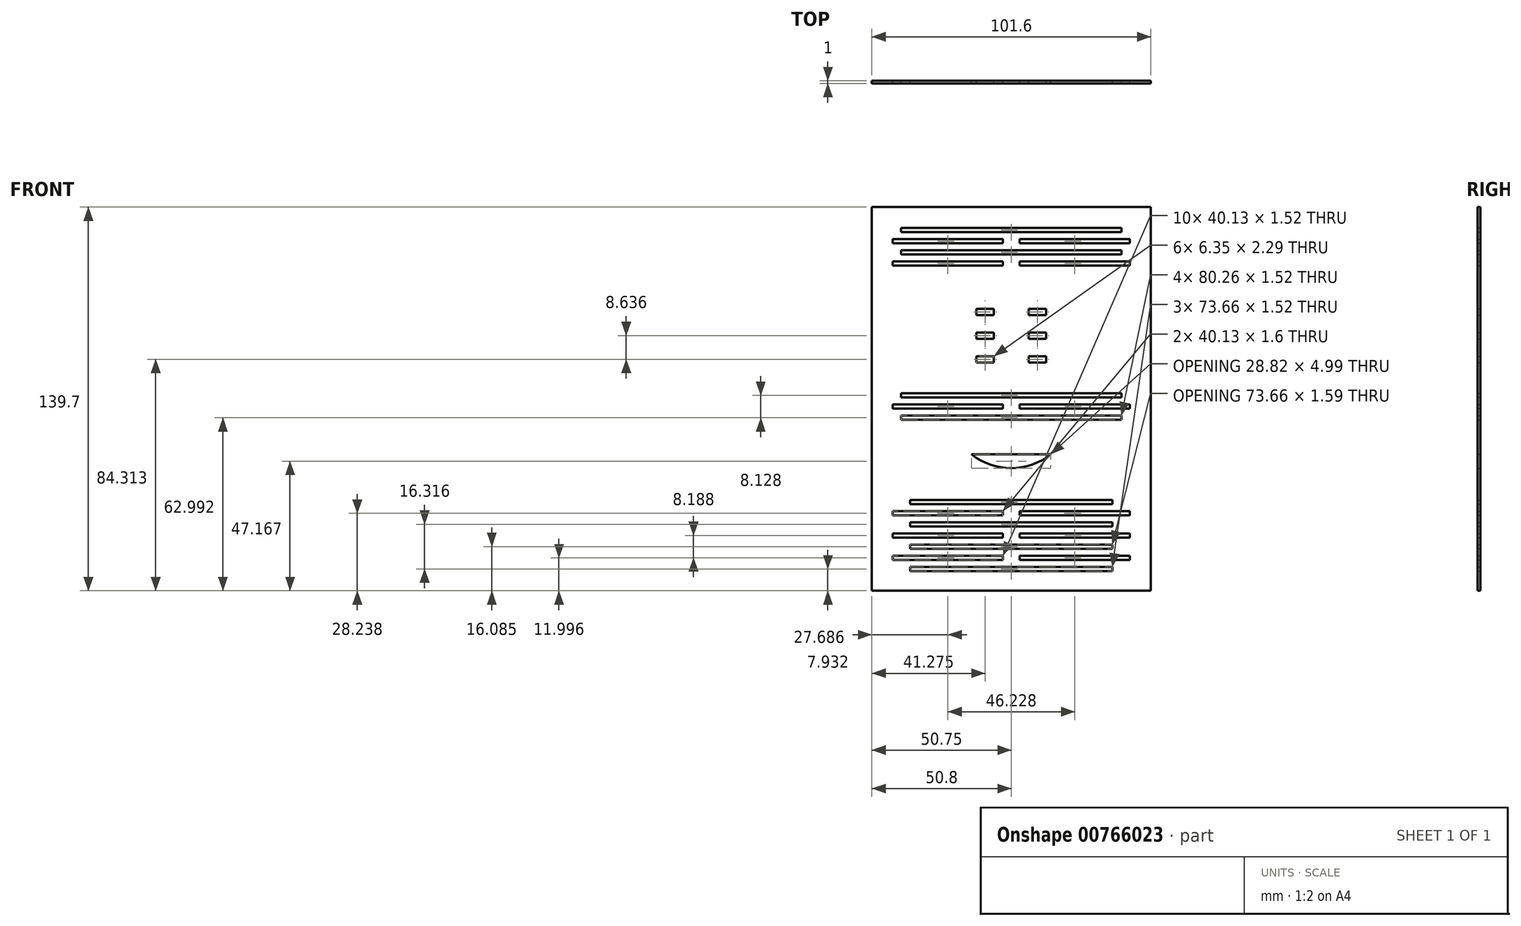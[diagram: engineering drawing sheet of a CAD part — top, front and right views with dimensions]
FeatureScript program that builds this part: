
annotation { "Feature Type Name" : "Feature", "Feature Type Description" : "" }
export const myFeature = defineFeature(function(context is Context, id is Id, definition is map)
    precondition{}
    {
        {
            var Q0;
            Q0=qCreatedBy(makeId("Front.planeOp"),FACE);
            var sketch = newSketch(context, id + "F0", { "sketchPlane" : qUnion([Q0])});
            skLineSegment(sketch, "E0.bottom", {"start": v(-50.8, 69.85) * mm, "end": v(50.8, 69.85) * mm});
            skLineSegment(sketch, "E0.top", {"start": v(-50.8, -69.85) * mm, "end": v(50.8, -69.85) * mm});
            skLineSegment(sketch, "E0.left", {"start": v(-50.8, 69.85) * mm, "end": v(-50.8, -69.85) * mm});
            skLineSegment(sketch, "E0.right", {"start": v(50.8, 69.85) * mm, "end": v(50.8, -69.85) * mm});
            skPoint(sketch, "E0.middle", {"position": v(0, 0) * mm});
            skLineSegment(sketch, "E1", {"start": v(-43.18, 62.23) * mm, "end": v(-43.18, -7.62) * mm});
            skLineSegment(sketch, "E2", {"start": v(43.18, 62.23) * mm, "end": v(43.18, -7.62) * mm});
            skLineSegment(sketch, "E3", {"start": v(-43.18, -20.19) * mm, "end": v(-43.18, -62.68) * mm});
            skLineSegment(sketch, "E4", {"start": v(-43.18, -20.19) * mm, "end": v(43.18, -20.19) * mm});
            skLineSegment(sketch, "E5", {"start": v(43.18, -20.19) * mm, "end": v(43.18, -62.68) * mm});
            skArc(sketch, "E6", {"start": v(-14.46, -20.19) * mm, "mid": v(-0.05, -25.18) * mm, "end": v(14.36, -20.19) * mm});
            skLineSegment(sketch, "E7", {"start": v(-43.18, 39.23) * mm, "end": v(-6.35, 39.23) * mm});
            skLineSegment(sketch, "E8.top", {"start": v(-6.35, 4.68) * mm, "end": v(6.35, 4.68) * mm});
            skLineSegment(sketch, "E8.left", {"start": v(-6.35, 39.23) * mm, "end": v(-6.35, 6.97) * mm});
            skLineSegment(sketch, "E8.right", {"start": v(6.35, 39.23) * mm, "end": v(6.35, 6.97) * mm});
            skLineSegment(sketch, "E9.trimOffspring", {"start": v(6.35, 39.23) * mm, "end": v(43.18, 39.23) * mm});
            skLineSegment(sketch, "E10.bottom", {"start": v(-6.35, 32.88) * mm, "end": v(-12.7, 32.88) * mm});
            skLineSegment(sketch, "E10.top", {"start": v(-6.35, 30.6) * mm, "end": v(-12.7, 30.6) * mm});
            skLineSegment(sketch, "E10.left", {"start": v(-6.35, 32.88) * mm, "end": v(-6.35, 30.6) * mm});
            skLineSegment(sketch, "E10.right", {"start": v(-12.7, 32.88) * mm, "end": v(-12.7, 30.6) * mm});
            skLineSegment(sketch, "E11.bottom", {"start": v(6.35, 32.88) * mm, "end": v(12.7, 32.88) * mm});
            skLineSegment(sketch, "E11.top", {"start": v(6.35, 30.6) * mm, "end": v(12.7, 30.6) * mm});
            skLineSegment(sketch, "E11.left", {"start": v(6.35, 32.88) * mm, "end": v(6.35, 30.6) * mm});
            skLineSegment(sketch, "E11.right", {"start": v(12.7, 32.88) * mm, "end": v(12.7, 30.6) * mm});
            skLineSegment(sketch, "E12.bottom", {"start": v(-6.35, 24.24) * mm, "end": v(-12.7, 24.24) * mm});
            skLineSegment(sketch, "E12.top", {"start": v(-6.35, 21.96) * mm, "end": v(-12.7, 21.96) * mm});
            skLineSegment(sketch, "E12.left", {"start": v(-6.35, 24.24) * mm, "end": v(-6.35, 21.96) * mm});
            skLineSegment(sketch, "E12.right", {"start": v(-12.7, 24.24) * mm, "end": v(-12.7, 21.96) * mm});
            skLineSegment(sketch, "E13.bottom", {"start": v(6.35, 24.24) * mm, "end": v(12.7, 24.24) * mm});
            skLineSegment(sketch, "E13.top", {"start": v(6.35, 21.96) * mm, "end": v(12.7, 21.96) * mm});
            skLineSegment(sketch, "E13.left", {"start": v(6.35, 24.24) * mm, "end": v(6.35, 21.96) * mm});
            skLineSegment(sketch, "E13.right", {"start": v(12.7, 24.24) * mm, "end": v(12.7, 21.96) * mm});
            skLineSegment(sketch, "E14.bottom", {"start": v(-6.35, 15.6) * mm, "end": v(-12.7, 15.6) * mm});
            skLineSegment(sketch, "E14.top", {"start": v(-6.35, 13.32) * mm, "end": v(-12.7, 13.32) * mm});
            skLineSegment(sketch, "E14.left", {"start": v(-6.35, 15.6) * mm, "end": v(-6.35, 13.32) * mm});
            skLineSegment(sketch, "E14.right", {"start": v(-12.7, 15.6) * mm, "end": v(-12.7, 13.32) * mm});
            skLineSegment(sketch, "E15.bottom", {"start": v(6.35, 15.6) * mm, "end": v(12.7, 15.6) * mm});
            skLineSegment(sketch, "E15.top", {"start": v(6.35, 13.32) * mm, "end": v(12.7, 13.32) * mm});
            skLineSegment(sketch, "E15.left", {"start": v(6.35, 15.6) * mm, "end": v(6.35, 13.32) * mm});
            skLineSegment(sketch, "E15.right", {"start": v(12.7, 15.6) * mm, "end": v(12.7, 13.32) * mm});
            skLineSegment(sketch, "E16.bottom", {"start": v(-6.35, 4.68) * mm, "end": v(-12.7, 4.68) * mm});
            skLineSegment(sketch, "E16.top", {"start": v(-6.35, 6.97) * mm, "end": v(-12.7, 6.97) * mm});
            skLineSegment(sketch, "E16.right", {"start": v(-12.7, 4.68) * mm, "end": v(-12.7, 6.97) * mm});
            skLineSegment(sketch, "E17.bottom", {"start": v(6.35, 4.68) * mm, "end": v(12.7, 4.68) * mm});
            skLineSegment(sketch, "E17.top", {"start": v(6.35, 6.97) * mm, "end": v(12.7, 6.97) * mm});
            skLineSegment(sketch, "E17.right", {"start": v(12.7, 4.68) * mm, "end": v(12.7, 6.97) * mm});
            skLineSegment(sketch, "E18.bottom", {"start": v(-36.83, -36.75) * mm, "end": v(36.83, -36.75) * mm});
            skLineSegment(sketch, "E18.top", {"start": v(-36.83, -38.27) * mm, "end": v(36.83, -38.27) * mm});
            skLineSegment(sketch, "E18.left", {"start": v(-36.83, -36.75) * mm, "end": v(-36.83, -38.27) * mm});
            skLineSegment(sketch, "E18.right", {"start": v(36.83, -36.75) * mm, "end": v(36.83, -38.27) * mm});
            skPoint(sketch, "E19.middle", {"position": v(0, -41.57) * mm});
            skPoint(sketch, "E20.left.start.orphan", {"position": v(-43.18, -42.41) * mm});
            skLineSegment(sketch, "E21.left", {"start": v(-43.18, -40.81) * mm, "end": v(-43.18, -42.34) * mm});
            skPoint(sketch, "E22.firstSnap0", {"position": v(43.18, -42.41) * mm});
            skPoint(sketch, "E22.firstSnap1", {"position": v(-21.59, -40.81) * mm});
            skPoint(sketch, "E22.oppositeSnap0", {"position": v(43.18, -42.41) * mm});
            skLineSegment(sketch, "E22.left", {"start": v(43.18, -40.81) * mm, "end": v(43.18, -42.41) * mm});
            skLineSegment(sketch, "E23.bottom", {"start": v(36.83, -46.36) * mm, "end": v(-36.83, -46.36) * mm});
            skLineSegment(sketch, "E23.top", {"start": v(36.83, -44.84) * mm, "end": v(-36.83, -44.84) * mm});
            skLineSegment(sketch, "E23.left", {"start": v(36.83, -46.36) * mm, "end": v(36.83, -44.84) * mm});
            skLineSegment(sketch, "E23.right", {"start": v(-36.83, -46.36) * mm, "end": v(-36.83, -44.84) * mm});
            skPoint(sketch, "E23.middle", {"position": v(0, -45.6) * mm});
            skPoint(sketch, "E24.middle", {"position": v(0, -49.81) * mm});
            skLineSegment(sketch, "E25.MirrorCS", {"start": v(-36.83, -46.36) * mm, "end": v(36.83, -46.36) * mm});
            skLineSegment(sketch, "E26.MirrorCS", {"start": v(-36.83, -44.84) * mm, "end": v(36.83, -44.84) * mm});
            skPoint(sketch, "E27.start.orphan", {"position": v(0, -40.81) * mm});
            skPoint(sketch, "E19.left.end.orphan", {"position": v(-12.2, -42.34) * mm});
            skPoint(sketch, "E19.left.start.orphan", {"position": v(-12.2, -40.81) * mm});
            skPoint(sketch, "E19.right.end.orphan", {"position": v(12.2, -42.34) * mm});
            skPoint(sketch, "E19.right.start.orphan", {"position": v(12.2, -40.81) * mm});
            skPoint(sketch, "E28.trimOffspring.end.orphan", {"position": v(43.18, -40.81) * mm});
            skPoint(sketch, "E22.right.end.orphan", {"position": v(18.54, -42.41) * mm});
            skLineSegment(sketch, "E29", {"start": v(-43.18, -40.81) * mm, "end": v(-3.05, -40.81) * mm});
            skLineSegment(sketch, "E30", {"start": v(-3.05, -40.81) * mm, "end": v(-3.05, -42.34) * mm});
            skLineSegment(sketch, "E31", {"start": v(-3.05, -42.34) * mm, "end": v(-43.18, -42.41) * mm});
            skLineSegment(sketch, "E32.MirrorCS", {"start": v(3.05, -40.81) * mm, "end": v(3.05, -42.34) * mm});
            skLineSegment(sketch, "E33.MirrorCS", {"start": v(43.18, -40.81) * mm, "end": v(3.05, -40.81) * mm});
            skLineSegment(sketch, "E34.MirrorCS", {"start": v(3.05, -42.34) * mm, "end": v(43.18, -42.41) * mm});
            skPoint(sketch, "E24.right.end.orphan", {"position": v(-12.2, -50.57) * mm});
            skPoint(sketch, "E24.right.start.orphan", {"position": v(-12.2, -49.05) * mm});
            skPoint(sketch, "E24.left.end.orphan", {"position": v(12.2, -50.57) * mm});
            skPoint(sketch, "E24.left.start.orphan", {"position": v(12.2, -49.05) * mm});
            skPoint(sketch, "E35", {"position": v(-19.6, -48.9) * mm});
            skLineSegment(sketch, "E36", {"start": v(-43.18, -48.9) * mm, "end": v(-3.05, -48.9) * mm});
            skLineSegment(sketch, "E37", {"start": v(-3.05, -48.9) * mm, "end": v(-3.05, -50.43) * mm});
            skLineSegment(sketch, "E38", {"start": v(-3.05, -50.43) * mm, "end": v(-43.18, -50.43) * mm});
            skLineSegment(sketch, "E39.MirrorCS", {"start": v(43.18, -48.9) * mm, "end": v(3.05, -48.9) * mm});
            skLineSegment(sketch, "E40.MirrorCS", {"start": v(3.05, -50.43) * mm, "end": v(43.18, -50.43) * mm});
            skLineSegment(sketch, "E41.MirrorCS", {"start": v(3.05, -48.9) * mm, "end": v(3.05, -50.43) * mm});
            skPoint(sketch, "E42", {"position": v(-19.5, -52.97) * mm});
            skLineSegment(sketch, "E43", {"start": v(0, -52.97) * mm, "end": v(-36.83, -53.04) * mm});
            skLineSegment(sketch, "E44", {"start": v(-36.83, -53.04) * mm, "end": v(-36.83, -54.56) * mm});
            skLineSegment(sketch, "E45", {"start": v(-36.83, -54.56) * mm, "end": v(0, -54.5) * mm});
            skLineSegment(sketch, "E46.MirrorCS", {"start": v(0, -52.97) * mm, "end": v(36.83, -53.04) * mm});
            skLineSegment(sketch, "E47.MirrorCS", {"start": v(36.83, -54.56) * mm, "end": v(0, -54.5) * mm});
            skLineSegment(sketch, "E48.MirrorCS", {"start": v(36.83, -53.04) * mm, "end": v(36.83, -54.56) * mm});
            skPoint(sketch, "E49", {"position": v(-32.19, -57.1) * mm});
            skLineSegment(sketch, "E50", {"start": v(-43.18, -57.1) * mm, "end": v(-3.05, -57.1) * mm});
            skLineSegment(sketch, "E51", {"start": v(-3.05, -57.1) * mm, "end": v(-3.05, -58.62) * mm});
            skLineSegment(sketch, "E52", {"start": v(-3.05, -58.62) * mm, "end": v(-43.18, -58.62) * mm});
            skLineSegment(sketch, "E53.MirrorCS", {"start": v(3.05, -57.1) * mm, "end": v(3.05, -58.62) * mm});
            skLineSegment(sketch, "E54.MirrorCS", {"start": v(43.18, -57.1) * mm, "end": v(3.05, -57.1) * mm});
            skLineSegment(sketch, "E55.MirrorCS", {"start": v(3.05, -58.62) * mm, "end": v(43.18, -58.62) * mm});
            skPoint(sketch, "E56", {"position": v(-17.9, -61.16) * mm});
            skLineSegment(sketch, "E57", {"start": v(0, -61.16) * mm, "end": v(-36.83, -61.16) * mm});
            skLineSegment(sketch, "E58", {"start": v(-36.83, -61.16) * mm, "end": v(-36.83, -62.68) * mm});
            skLineSegment(sketch, "E59", {"start": v(-36.83, -62.68) * mm, "end": v(0, -62.68) * mm});
            skLineSegment(sketch, "E60.MirrorCS", {"start": v(0, -61.16) * mm, "end": v(36.83, -61.16) * mm});
            skLineSegment(sketch, "E61.MirrorCS", {"start": v(36.83, -62.68) * mm, "end": v(0, -62.68) * mm});
            skLineSegment(sketch, "E62.MirrorCS", {"start": v(36.83, -61.16) * mm, "end": v(36.83, -62.68) * mm});
            skPoint(sketch, "E63", {"position": v(-43.18, -62.68) * mm});
            skPoint(sketch, "E64.orphan", {"position": v(-43.18, -64.64) * mm});
            skPoint(sketch, "E65", {"position": v(43.18, -62.68) * mm});
            skPoint(sketch, "E66.orphan", {"position": v(43.18, -64.64) * mm});
            skPoint(sketch, "E67", {"position": v(0, -7.62) * mm});
            skLineSegment(sketch, "E68", {"start": v(0, -7.62) * mm, "end": v(-40.13, -7.62) * mm});
            skLineSegment(sketch, "E69", {"start": v(-40.13, -7.62) * mm, "end": v(-40.13, -6.1) * mm});
            skLineSegment(sketch, "E70", {"start": v(-40.13, -6.1) * mm, "end": v(0, -6.1) * mm});
            skLineSegment(sketch, "E71.MirrorCS", {"start": v(40.13, -6.1) * mm, "end": v(0, -6.1) * mm});
            skLineSegment(sketch, "E72.MirrorCS", {"start": v(0, -7.62) * mm, "end": v(40.13, -7.62) * mm});
            skLineSegment(sketch, "E73.MirrorCS", {"start": v(40.13, -7.62) * mm, "end": v(40.13, -6.1) * mm});
            skPoint(sketch, "E74", {"position": v(-6.23, -3.56) * mm});
            skLineSegment(sketch, "E75", {"start": v(-43.18, -3.56) * mm, "end": v(-3.05, -3.56) * mm});
            skLineSegment(sketch, "E76", {"start": v(-3.05, -3.56) * mm, "end": v(-3.05, -2.03) * mm});
            skLineSegment(sketch, "E77", {"start": v(-3.05, -2.03) * mm, "end": v(-43.18, -2.03) * mm});
            skLineSegment(sketch, "E78.MirrorCS", {"start": v(3.05, -2.03) * mm, "end": v(43.18, -2.03) * mm});
            skLineSegment(sketch, "E79.MirrorCS", {"start": v(43.18, -3.56) * mm, "end": v(3.05, -3.56) * mm});
            skLineSegment(sketch, "E80.MirrorCS", {"start": v(3.05, -3.56) * mm, "end": v(3.05, -2.03) * mm});
            skPoint(sketch, "E81", {"position": v(-12.52, 0.5) * mm});
            skLineSegment(sketch, "E82", {"start": v(0, 0.5) * mm, "end": v(-40.13, 0.5) * mm});
            skLineSegment(sketch, "E83", {"start": v(-40.13, 0.5) * mm, "end": v(-40.13, 2.03) * mm});
            skLineSegment(sketch, "E84", {"start": v(-40.13, 2.03) * mm, "end": v(0, 2.03) * mm});
            skLineSegment(sketch, "E85.MirrorCS", {"start": v(40.13, 2.03) * mm, "end": v(0, 2.03) * mm});
            skLineSegment(sketch, "E86.MirrorCS", {"start": v(0, 0.5) * mm, "end": v(40.13, 0.5) * mm});
            skLineSegment(sketch, "E87.MirrorCS", {"start": v(40.13, 0.5) * mm, "end": v(40.13, 2.03) * mm});
            skPoint(sketch, "E88", {"position": v(0, 62.23) * mm});
            skLineSegment(sketch, "E89", {"start": v(0, 62.23) * mm, "end": v(-40.13, 62.23) * mm});
            skLineSegment(sketch, "E90", {"start": v(-40.13, 62.23) * mm, "end": v(-40.13, 60.7) * mm});
            skLineSegment(sketch, "E91", {"start": v(-40.13, 60.7) * mm, "end": v(0, 60.7) * mm});
            skLineSegment(sketch, "E92.MirrorCS", {"start": v(0, 62.23) * mm, "end": v(40.13, 62.23) * mm});
            skLineSegment(sketch, "E93.MirrorCS", {"start": v(40.13, 62.23) * mm, "end": v(40.13, 60.7) * mm});
            skLineSegment(sketch, "E94.MirrorCS", {"start": v(40.13, 60.7) * mm, "end": v(0, 60.7) * mm});
            skPoint(sketch, "E95", {"position": v(-24.17, 58.17) * mm});
            skLineSegment(sketch, "E96", {"start": v(-43.18, 58.17) * mm, "end": v(-3.05, 58.17) * mm});
            skLineSegment(sketch, "E97", {"start": v(-3.05, 58.17) * mm, "end": v(-3.05, 56.64) * mm});
            skLineSegment(sketch, "E98", {"start": v(-3.05, 56.64) * mm, "end": v(-43.18, 56.64) * mm});
            skLineSegment(sketch, "E99.MirrorCS", {"start": v(3.05, 58.17) * mm, "end": v(3.05, 56.64) * mm});
            skLineSegment(sketch, "E100.MirrorCS", {"start": v(43.18, 58.17) * mm, "end": v(3.05, 58.17) * mm});
            skLineSegment(sketch, "E101.MirrorCS", {"start": v(3.05, 56.64) * mm, "end": v(43.18, 56.64) * mm});
            skPoint(sketch, "E102", {"position": v(-4.22, 54.1) * mm});
            skLineSegment(sketch, "E103", {"start": v(0, 54.1) * mm, "end": v(-40.13, 54.1) * mm});
            skLineSegment(sketch, "E104", {"start": v(-40.13, 54.1) * mm, "end": v(-40.13, 52.58) * mm});
            skLineSegment(sketch, "E105", {"start": v(-40.13, 52.58) * mm, "end": v(0, 52.58) * mm});
            skLineSegment(sketch, "E106.MirrorCS", {"start": v(0, 54.1) * mm, "end": v(40.13, 54.1) * mm});
            skLineSegment(sketch, "E107.MirrorCS", {"start": v(40.13, 54.1) * mm, "end": v(40.13, 52.58) * mm});
            skLineSegment(sketch, "E108.MirrorCS", {"start": v(40.13, 52.58) * mm, "end": v(0, 52.58) * mm});
            skPoint(sketch, "E109", {"position": v(-16.98, 50.04) * mm});
            skLineSegment(sketch, "E110", {"start": v(-43.18, 50.04) * mm, "end": v(-3.05, 50.04) * mm});
            skLineSegment(sketch, "E111", {"start": v(-3.05, 50.04) * mm, "end": v(-3.05, 48.51) * mm});
            skLineSegment(sketch, "E112", {"start": v(-3.05, 48.51) * mm, "end": v(-43.18, 48.51) * mm});
            skLineSegment(sketch, "E113.MirrorCS", {"start": v(43.18, 50.04) * mm, "end": v(3.05, 50.04) * mm});
            skLineSegment(sketch, "E114.MirrorCS", {"start": v(3.05, 50.04) * mm, "end": v(3.05, 48.51) * mm});
            skLineSegment(sketch, "E115.MirrorCS", {"start": v(3.05, 48.51) * mm, "end": v(43.18, 48.51) * mm});
            skSolve(sketch);
        }
        {
            var Q0;
            Q0 = qSketchRegion(id + "F0", true);
            extrude(context, id + "F1", {"entities" : qUnion([Q0]), "depth" : 1 * mm, "offsetDistance" : 25 * mm});
        }
    });
